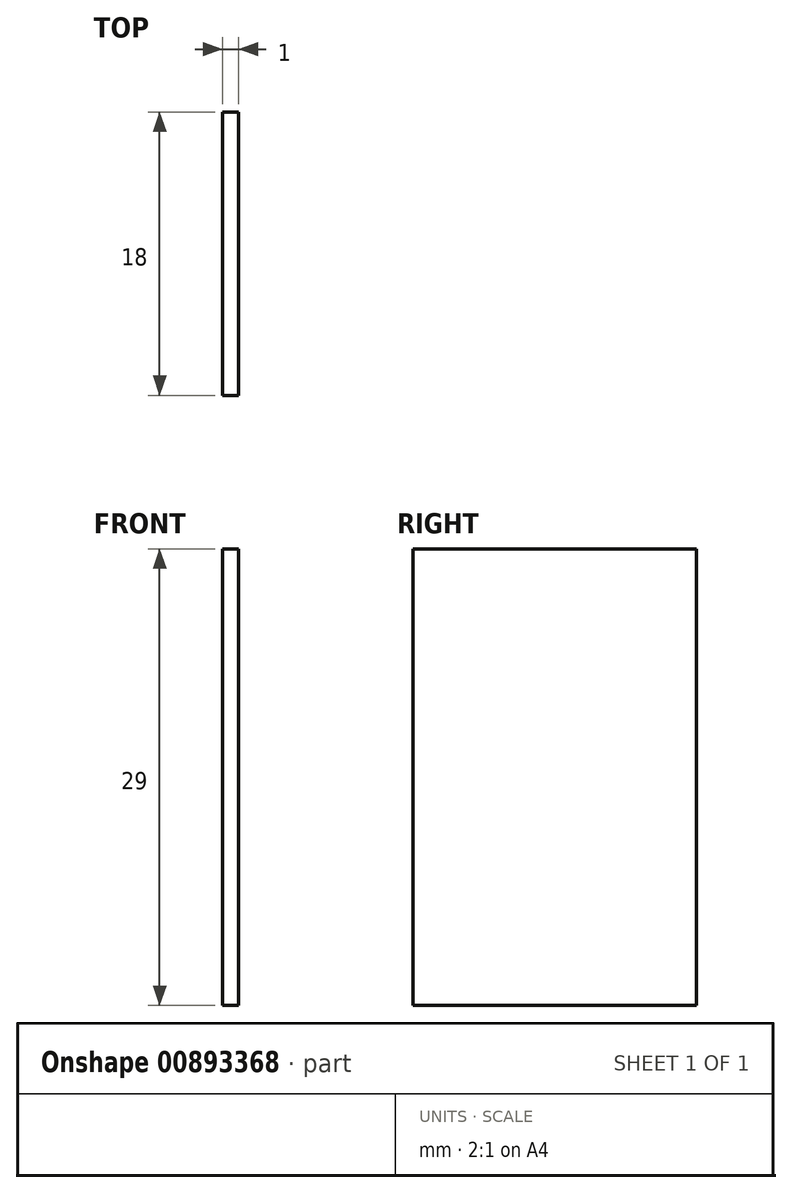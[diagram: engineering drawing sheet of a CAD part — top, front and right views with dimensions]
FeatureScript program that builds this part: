
annotation { "Feature Type Name" : "Feature", "Feature Type Description" : "" }
export const myFeature = defineFeature(function(context is Context, id is Id, definition is map)
    precondition{}
    {
        {
            var Q0;
            Q0=qCreatedBy(makeId("Right.planeOp"),FACE);
            var sketch = newSketch(context, id + "F0", { "sketchPlane" : qUnion([Q0])});
            skLineSegment(sketch, "E0.bottom", {"start": v(9, 14.5) * mm, "end": v(-9, 14.5) * mm});
            skLineSegment(sketch, "E0.top", {"start": v(9, -14.5) * mm, "end": v(-9, -14.5) * mm});
            skLineSegment(sketch, "E0.left", {"start": v(9, 14.5) * mm, "end": v(9, -14.5) * mm});
            skLineSegment(sketch, "E0.right", {"start": v(-9, 14.5) * mm, "end": v(-9, -14.5) * mm});
            skPoint(sketch, "E0.middle", {"position": v(0, 0) * mm});
            skSolve(sketch);
        }
        {
            var Q0;
            Q0=makeQuery(id+"F0.imprint","IMPRINT",FACE,{"disambiguationData":[TD([[makeQuery(id+"F0.imprint","IMPRINT",EDGE,{"derivedFrom":sQuery(id+"F0.wireOp",EDGE,"E0.bottom")}),1.0]])]});
            extrude(context, id + "F1", {"entities" : qUnion([Q0]), "depth" : 1 * mm, "offsetDistance" : 25 * mm});
        }
    });
